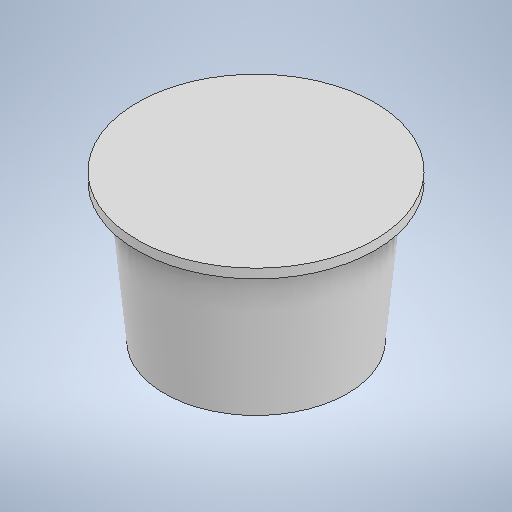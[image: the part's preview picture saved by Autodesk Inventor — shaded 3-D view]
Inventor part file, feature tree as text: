
AUTODESK INVENTOR PART (.ipt)
format: ipt  version: 2025 (Build 290162000, 162)  size: 210,432 bytes
history: native  units: in
note: dims shown in document units (in); Inventor stores cm internally (conversion verified against a paired STEP export)
features: revolve x1, sketch x1
ambient origin geometry x8: Origin, YZ Plane, XZ Plane, XY Plane, X Axis, Y Axis, Z Axis, Center Point
bodies: Solid1 (feature_tree)
feature tree (2):
  revolve  "Revolution1"  [1 undecoded]
  sketch  "Sketch1"  dims[d0=0.3248in d1=0.25in d2=0.4016in d3=90.0deg]
note: 1 required parameter value undecoded (feature->parameter linkage not recoverable at this tier; creation-order binding heuristic only, values carry confidence <= 0.55)
